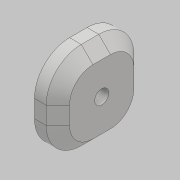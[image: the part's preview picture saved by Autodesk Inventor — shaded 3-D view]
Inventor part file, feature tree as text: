
AUTODESK INVENTOR PART (.ipt)
format: ipt  version: 2018 (Build 220112000, 112)  size: 134,144 bytes
history: native  units: mm
features: sketch x3, hole x2, other x1, extrude x1, fillet x1, chamfer x1, projected_geometry x1
ambient origin geometry x8: Origin, YZ Plane, XZ Plane, XY Plane, X Axis, Y Axis, Z Axis, Center Point
bodies: Body1 (feature_tree)
feature tree (10):
  other  "實體1"
  extrude  "擠出1"  Depth=75.0mm
  fillet  "圓角1"  Radius=75.0mm
  chamfer  "倒角1"  Distance=20.0mm
  hole  "孔1"  [1 undecoded]
  hole  "孔2"  [1 undecoded]
  sketch  "草圖1"
  sketch  "草圖2"
  sketch  "草圖3"
  projected_geometry  "投影迴路1"
note: 2 required parameter values undecoded (feature->parameter linkage not recoverable at this tier; creation-order binding heuristic only, values carry confidence <= 0.55)
